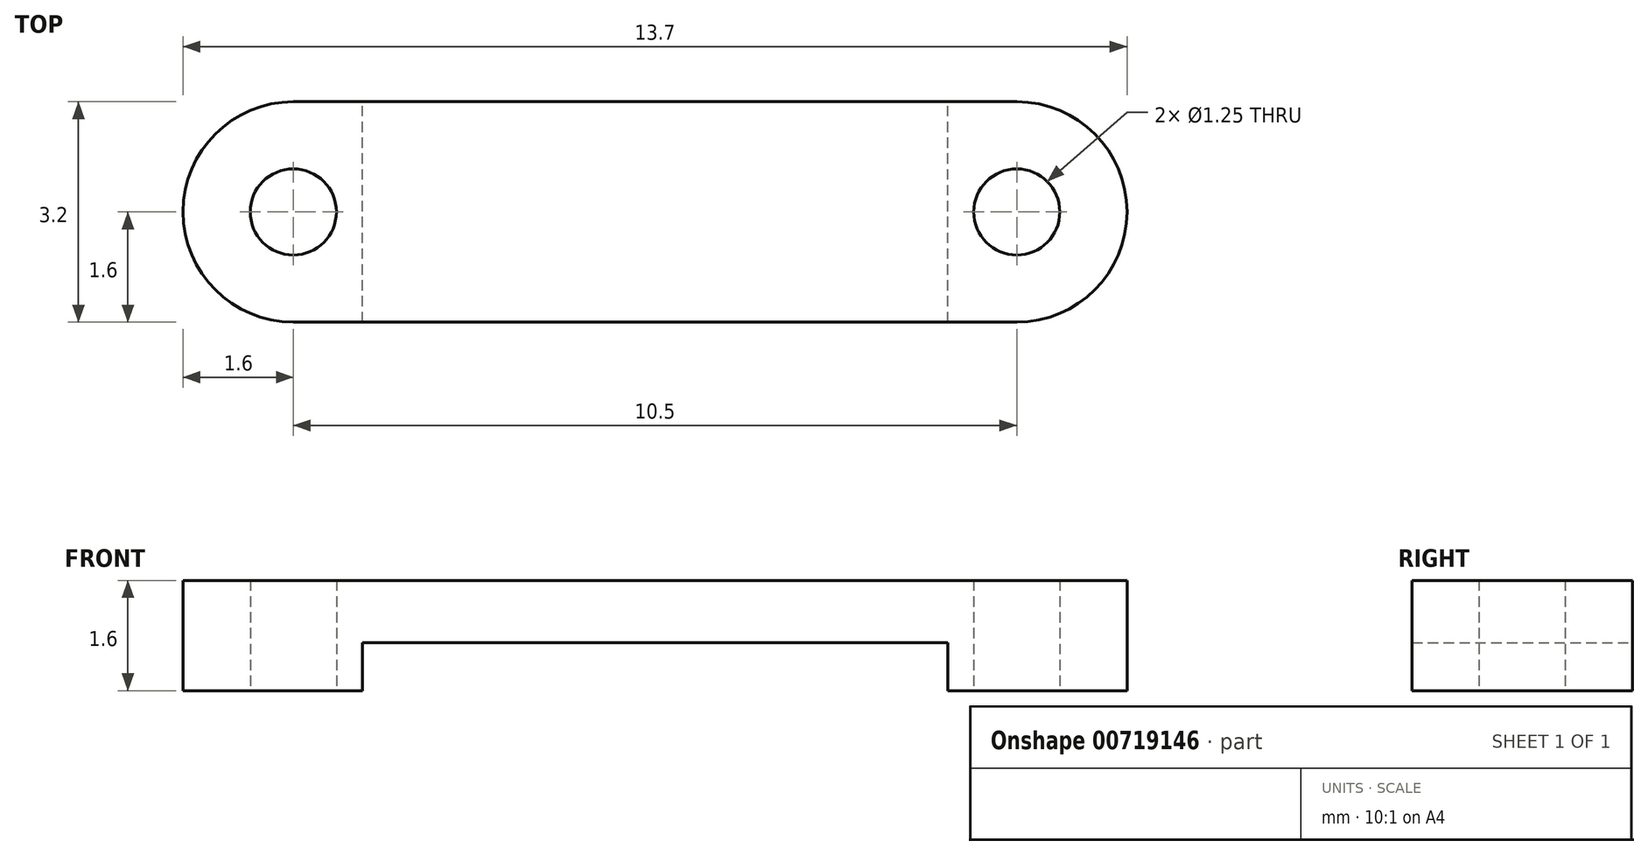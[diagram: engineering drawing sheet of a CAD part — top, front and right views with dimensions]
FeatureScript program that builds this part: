
annotation { "Feature Type Name" : "Feature", "Feature Type Description" : "" }
export const myFeature = defineFeature(function(context is Context, id is Id, definition is map)
    precondition{}
    {
        {
            var Q0;
            Q0=qCreatedBy(makeId("Top.planeOp"),FACE);
            var sketch = newSketch(context, id + "F0", { "sketchPlane" : qUnion([Q0])});
            skCircle(sketch, "E0", {"center": v(0, 0) * mm, "radius": 0.62 * mm});
            skCircle(sketch, "E1", {"center": v(10.5, 0) * mm, "radius": 0.62 * mm});
            skArc(sketch, "E2", {"start": v(0, 1.6) * mm, "mid": v(-1.6, 0) * mm, "end": v(0, -1.6) * mm});
            skLineSegment(sketch, "E3.bottom", {"start": v(0, 1.6) * mm, "end": v(10.5, 1.6) * mm});
            skLineSegment(sketch, "E3.top", {"start": v(0, -1.6) * mm, "end": v(10.5, -1.6) * mm});
            skArc(sketch, "E4", {"start": v(10.5, -1.6) * mm, "mid": v(12.1, 0) * mm, "end": v(10.5, 1.6) * mm});
            skSolve(sketch);
        }
        {
            var Q0;
            Q0=qSketchRegion(id+"F0",true);
            extrude(context, id + "F1", {"entities" : qUnion([Q0]), "depth" : 1.6 * mm, "offsetDistance" : 25 * mm});
        }
        {
            var Q0;
            Q0=makeQuery(id+"F1.opExtrude","CAP_FACE",FACE,{"disambiguationData":[OSD([sQuery(id+"F0.wireOp",EDGE,"E0"),sQuery(id+"F0.wireOp",EDGE,"E1"),sQuery(id+"F0.wireOp",EDGE,"E2"),sQuery(id+"F0.wireOp",EDGE,"E3.bottom"),sQuery(id+"F0.wireOp",EDGE,"E3.top"),sQuery(id+"F0.wireOp",EDGE,"E4")])],"isStart":true});
            var sketch = newSketch(context, id + "F2", { "sketchPlane" : qUnion([Q0])});
            skLineSegment(sketch, "E5.bottom", {"start": v(1, 1.6) * mm, "end": v(9.5, 1.6) * mm});
            skLineSegment(sketch, "E5.top", {"start": v(1, -1.6) * mm, "end": v(9.5, -1.6) * mm});
            skLineSegment(sketch, "E5.left", {"start": v(1, 1.6) * mm, "end": v(1, -1.6) * mm});
            skLineSegment(sketch, "E5.right", {"start": v(9.5, 1.6) * mm, "end": v(9.5, -1.6) * mm});
            skLineSegment(sketch, "E6", {"start": v(5.25, 1.6) * mm, "end": v(5.25, -0.47) * mm, "construction": true});
            skSolve(sketch);
        }
        {
            var Q0;
            Q0=qSketchRegion(id+"F2",true);
            extrude(context, id + "F3", {"entities" : qUnion([Q0]), "operationType" : NewBodyOperationType.REMOVE, "oppositeDirection" : true, "depth" : 0.7 * mm, "offsetDistance" : 25 * mm});
        }
    });
